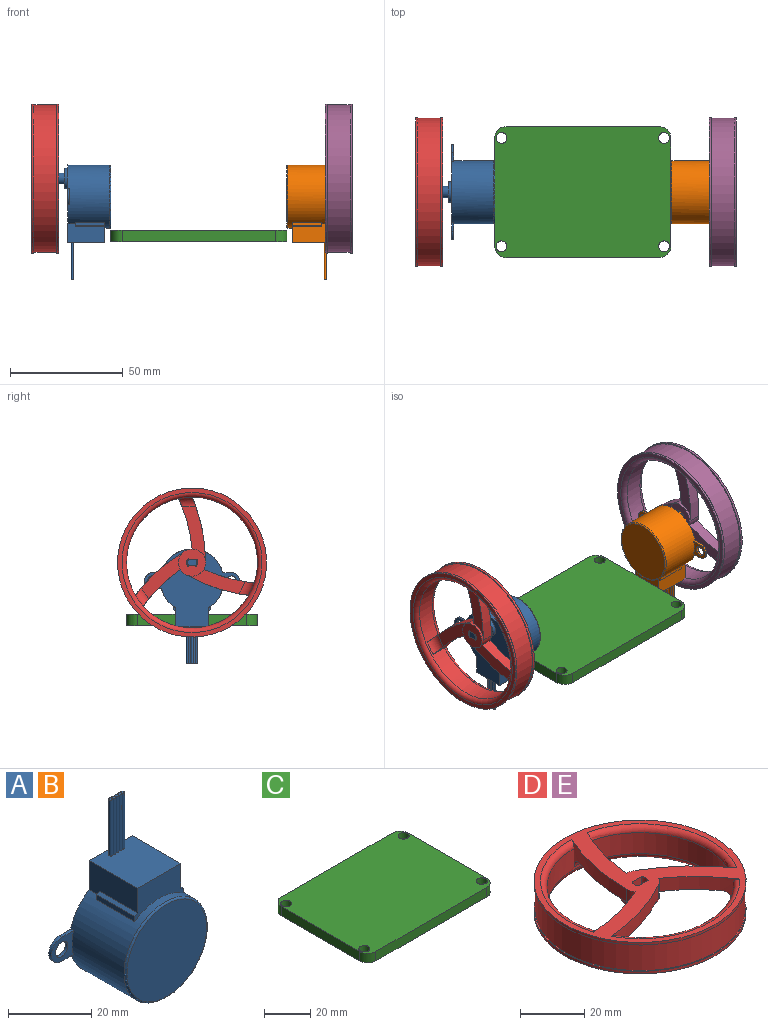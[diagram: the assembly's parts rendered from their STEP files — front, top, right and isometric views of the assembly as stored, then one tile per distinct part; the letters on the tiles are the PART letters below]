
ASSEMBLY  parts=5 mates=4
PART A: 44 faces, bbox 42.2x29.2x52.3 mm
  f0: torus R=13.5mm, axis (0,1,0), area 68.2mm2, adj f9,f14
  f1: cylinder r=4.5mm len=9mm, axis (0,-1,0), area 42.4mm2, adj f13,f37
  f2: cylinder r=0.48mm len=16.4mm, axis (0,0,-1), area 49.5mm2, adj f25,f30
  f3: cylinder r=0.48mm len=16.4mm, axis (0,0,-1), area 49.5mm2, adj f25,f29
  f4: cylinder r=0.48mm len=16.4mm, axis (0,0,-1), area 49.5mm2, adj f25,f28
  f5: cylinder r=0.48mm len=16.4mm, axis (0,0,-1), area 49.5mm2, adj f25,f27
  f6: cylinder r=0.48mm len=16.4mm, axis (0,0,-1), area 49.5mm2, adj f25,f26
  f7: cylinder r=2.1mm len=4.2mm, axis (0,1,0), area 11.9mm2, adj f13,f22
  f8: cylinder r=2.1mm len=4.2mm, axis (0,1,0), area 11.9mm2, adj f13,f18
  f9: cylinder r=14mm len=28mm, axis (0,-1,0), area 1331.6mm2, adj f0,f12,f13,f16,f17,f18,f20,f21
  f10: cylinder r=2.5mm len=8mm, axis (0,-1,0), area 74.7mm2, adj f37,f38,f39,f40,f41,f42,f43
  f11: plane 4x3mm, normal (0,1,0), area 10.8mm2, adj f38,f41,f42,f43
  f12: plane 16.6x9.23mm, normal (0,-1,0), area 107.4mm2, adj f9,f23,f24,f25,f31,f32,f34,f35
  f13: plane 42x34.5mm, normal (0,1,0), area 718.6mm2, adj f1,f7,f8,f9,f15,f16,f17,f19
  f14: plane 27x27mm, normal (0,-1,0), area 572.6mm2, adj f0
  f15: cylinder r=3.5mm len=7mm, axis (0,1,0), area 9.9mm2, adj f13,f16,f17,f18
  f16: plane 3.94x0.9mm, normal (0,0,-1), area 3.6mm2, adj f9,f13,f15,f18
  f17: plane 3.94x0.9mm, normal (0,0,1), area 3.6mm2, adj f9,f13,f15,f18
  f18: plane 7.44x7mm, normal (0,-1,0), area 30.9mm2, adj f8,f9,f15,f16,f17
  f19: cylinder r=3.5mm len=7mm, axis (0,1,0), area 9.9mm2, adj f13,f20,f21,f22
  f20: plane 3.94x0.9mm, normal (0,0,1), area 3.6mm2, adj f9,f13,f19,f22
  f21: plane 3.94x0.9mm, normal (0,0,-1), area 3.6mm2, adj f9,f13,f19,f22
  f22: plane 7.44x7mm, normal (0,-1,0), area 30.9mm2, adj f7,f9,f19,f20,f21
  f23: plane 16.4x8.55mm, normal (-1,0,0), area 122.8mm2, adj f9,f12,f13,f25,f31,f33
  f24: plane 16.4x8.55mm, normal (1,0,0), area 122.8mm2, adj f9,f12,f13,f25,f35,f36
  f25: plane 16.4x14.6mm, normal (0,0,1), area 235.8mm2, adj f2,f3,f4,f5,f6,f12,f13,f23
  f26: plane 0.96x0.96mm, normal (0,0,1), area 0.7mm2, adj f6
  f27: plane 0.96x0.96mm, normal (0,0,1), area 0.7mm2, adj f5
  f28: plane 0.96x0.96mm, normal (0,0,1), area 0.7mm2, adj f4
  f29: plane 0.96x0.96mm, normal (0,0,1), area 0.7mm2, adj f3
  f30: plane 0.96x0.96mm, normal (0,0,1), area 0.7mm2, adj f2
  f31: plane 12.9x1mm, normal (-0.47,0,0.88), area 14.6mm2, adj f12,f23,f32,f33
  f32: plane 12.9x1.5mm, normal (-1,0,0), area 19.3mm2, adj f9,f12,f31,f33
  f33: plane 2.03x1mm, normal (0,1,0), area 1.4mm2, adj f9,f23,f31,f32
  f34: plane 12.9x1.5mm, normal (1,0,0), area 19.3mm2, adj f9,f12,f35,f36
  f35: plane 12.9x1mm, normal (0.47,0,0.88), area 14.6mm2, adj f12,f24,f34,f36
  f36: plane 2.03x1mm, normal (0,1,0), area 1.4mm2, adj f9,f24,f34,f35
  f37: plane 9x9mm, normal (0,1,0), area 44mm2, adj f1,f10
  f38: plane 6.22x4.22mm, normal (0,0,-1), area 23.9mm2, adj f10,f11,f39,f42,f43
  f39: plane 4x1mm, normal (0,1,0), area 2.8mm2, adj f10,f38
  f40: plane 4x1mm, normal (0,1,0), area 2.8mm2, adj f10,f41
  f41: plane 6.22x4.22mm, normal (0,0,1), area 23.9mm2, adj f10,f11,f40,f42,f43
  f42: torus R=2mm, axis (0,1,0), area 2.7mm2, adj f10,f11,f38,f41
  f43: torus R=2mm, axis (0,1,0), area 2.7mm2, adj f10,f11,f38,f41
PART B: same geometry as A
PART C: 14 faces, bbox 78x58x5 mm
  f0: plane 48x5mm, normal (-1,0,0), area 240mm2, adj f1,f11,f12,f13
  f1: cylinder r=5mm len=5mm, axis (0,0,-1), area 39.3mm2, adj f0,f2,f12,f13
  f2: plane 68x5mm, normal (0,-1,0), area 340mm2, adj f1,f3,f12,f13
  f3: cylinder r=5mm len=5mm, axis (0,0,-1), area 39.3mm2, adj f2,f4,f12,f13
  f4: plane 48x5mm, normal (1,0,0), area 240mm2, adj f3,f5,f12,f13
  f5: cylinder r=5mm len=5mm, axis (0,0,-1), area 39.3mm2, adj f4,f6,f12,f13
  f6: plane 68x5mm, normal (0,1,0), area 340mm2, adj f5,f11,f12,f13
  f7: cylinder r=2.4mm len=5mm, axis (0,0,-1), area 75.4mm2, adj f12,f13
  f8: cylinder r=2.4mm len=5mm, axis (0,0,-1), area 75.4mm2, adj f12,f13
  f9: cylinder r=2.4mm len=5mm, axis (0,0,-1), area 75.4mm2, adj f12,f13
  f10: cylinder r=2.4mm len=5mm, axis (0,0,-1), area 75.4mm2, adj f12,f13
  f11: cylinder r=5mm len=5mm, axis (0,0,-1), area 39.3mm2, adj f0,f6,f12,f13
  f12: plane 78x58mm, normal (0,0,1), area 4430.2mm2, adj f0,f1,f2,f3,f4,f5,f6,f7
  f13: plane 78x58mm, normal (0,0,-1), area 4430.2mm2, adj f0,f1,f2,f3,f4,f5,f6,f7
PART D: 30 faces, bbox 70.2x70.2x12 mm
  f0: cylinder r=33mm len=66mm, axis (0,0,1), area 207.3mm2, adj f3,f27
  f1: plane 12x12mm, normal (0,0,-1), area 99.1mm2, adj f2,f4,f5,f6,f7
  f2: plane 6x4mm, normal (0,-1,0), area 24mm2, adj f1,f3,f5,f6
  f3: plane 66x66mm, normal (0,0,1), area 966mm2, adj f0,f2,f4,f5,f6,f7,f8,f9
  f4: cylinder r=6mm len=12mm, axis (0,0,1), area 84.8mm2, adj f1,f3,f8,f9,f10,f11,f12,f13
  f5: cylinder r=2.5mm len=6mm, axis (0,0,1), area 19.3mm2, adj f1,f2,f3,f7
  f6: cylinder r=2.5mm len=6mm, axis (0,0,1), area 19.3mm2, adj f1,f2,f3,f7
  f7: plane 6x4mm, normal (0,1,0), area 24mm2, adj f1,f3,f5,f6
  f8: cylinder r=73.08mm len=30.99mm, axis (0,0,1), area 153.8mm2, adj f3,f4,f10,f17,f21,f25
  f9: cylinder r=67.35mm len=24.22mm, axis (0,0,1), area 120.8mm2, adj f3,f4,f10,f17,f21,f23
  f10: plane 25x10.39mm, normal (0,0,-1), area 118.7mm2, adj f4,f8,f9,f21
  f11: cylinder r=73.08mm len=30.28mm, axis (0,0,1), area 153.8mm2, adj f3,f4,f13,f17,f22,f24
  f12: cylinder r=67.35mm len=24.43mm, axis (0,0,1), area 120.8mm2, adj f3,f4,f13,f17,f22,f25
  f13: plane 26.51x10.87mm, normal (0,0,-1), area 118.7mm2, adj f4,f11,f12,f22
  f14: cylinder r=73.08mm len=23.39mm, axis (0,0,1), area 153.8mm2, adj f3,f4,f16,f17,f20,f23
  f15: cylinder r=67.35mm len=18.08mm, axis (0,0,1), area 120.8mm2, adj f3,f4,f16,f17,f20,f24
  f16: plane 21.3x19.41mm, normal (0,0,-1), area 118.7mm2, adj f4,f14,f15,f20
  f17: cylinder r=29mm len=58mm, axis (0,0,1), area 1330.8mm2, adj f8,f9,f11,f12,f14,f15,f20,f21
  f18: cylinder r=33mm len=66mm, axis (0,0,1), area 207.3mm2, adj f19,f29
  f19: plane 66x66mm, normal (0,0,-1), area 402.1mm2, adj f18,f26
  f20: torus R=25mm, axis (0,0,1), area 37.9mm2, adj f14,f15,f16,f17
  f21: torus R=25mm, axis (0,0,1), area 37.9mm2, adj f8,f9,f10,f17
  f22: torus R=25mm, axis (0,0,1), area 37.9mm2, adj f11,f12,f13,f17
  f23: torus R=31mm, axis (0,0,1), area 176.6mm2, adj f3,f9,f14,f17
  f24: torus R=31mm, axis (0,0,1), area 176.6mm2, adj f3,f11,f15,f17
  f25: torus R=31mm, axis (0,0,1), area 176.6mm2, adj f3,f8,f12,f17
  f26: torus R=31mm, axis (0,0,1), area 586.8mm2, adj f17,f19
  f27: plane 66x66mm, normal (0,0,-1), area 82.4mm2, adj f0,f28
  f28: cylinder r=32.6mm len=65.2mm, axis (0,0,1), area 2048.3mm2, adj f27,f29
  f29: plane 66x66mm, normal (0,0,1), area 82.4mm2, adj f18,f28
PART E: same geometry as D
PLACE A rot(axis=(0.71,-0.71,0),180deg) t=(-39,0,20)mm
PLACE B rot(axis=(0.71,0.71,0),180deg) t=(39,0,20)mm
PLACE C at identity
PLACE D rot(axis=(0.58,0.58,0.58),120deg) t=(-62,0,28)mm
PLACE E rot(axis=(0.58,0.58,0.58),120deg) t=(68,0,28)mm
MATE fastened B.f0 <-> C.f4  axis (-1,0,0) through (39,0,20)mm
MATE fastened A.f0 <-> C.f0  axis (1,0,0) through (-39,0,20)mm
MATE fastened B.f1 <-> E.f0  axis (1,0,0) through (68,0,28)mm
MATE fastened D.f4 <-> A.f1  axis (-1,0,0) through (-68,0,28)mm
